# Revit family: Shower-Valve_Trim-KALLISTA-Capsule-P34130
name_source: partatom
category: Specialty Equipment
units: mm (PartAtom-declared; Revit-internal decimal feet)

## family parameters
Cut with Voids When Loaded = No
Host = Face
OmniClass Number = 23.31.25.00
OmniClass Title = Toilet and Bath Specialties
Part Type = Normal
Room Calculation Point = No
Round Connector Dimension = Use Diameter
Shared = No

## types (6) — shared parameters
ADA Compliant = No
Assembly Code = C1030200
Date Modified = 12/31/2024
Default Elevation = 42"
Description = Pressure Balance Trim, Lever
Handle Clearance = 3 1/8"
Height = 6 1/4"
Length = 3 11/16"
Manufacturer = Kallista Co.
Master Format 2014 = 10 28 00
Master Format 2014 Name = Toilet, Bath, and Laundry Accessories
Material = Premium Metal Construction
Product Documentation Link = https://resources.kohler.com
Product Name = Capsule
URL = https://www.kallista.com
WaterSense Certified = No
Width = 6 1/4"

## per-type parameters (varying)
| type | Finish | Model | Product Page URL | Type |
| BAF-Brushed French Gold | Kallista-Metal-BAF-Brushed_French_Gold | P34130-LV-BAF | https://www.kallista.com | 1 |
| BL-Matte Black | Kalista-Metal-BL-Matte_Black | P34130-LV-BL | https://www.kallista.com | 2 |
| BN-Brushed Nickel | Kallista-Metal-BN-Brushed_Nickel | P34130-LV-BN | https://www.kallista.com | 3 |
| CP-Chrome | Kallista-Metal-CP-Chrome | P34130-LV-CP | https://www.kallista.com | 4 |
| SN-Polished Nickel | Kallista-Metal-SN-Polished_Nickel | P34130-LV-SN | https://www.kallista.com | 5 |
| 2MB-Brushed Brass | Kallista-Metal-2MB-Brushed_Brass | P34130-LV-2MB |  | 6 |

## geometry (parser evidence)
native form markers: Sweep x6
no freeform markers — native parametric forms only
